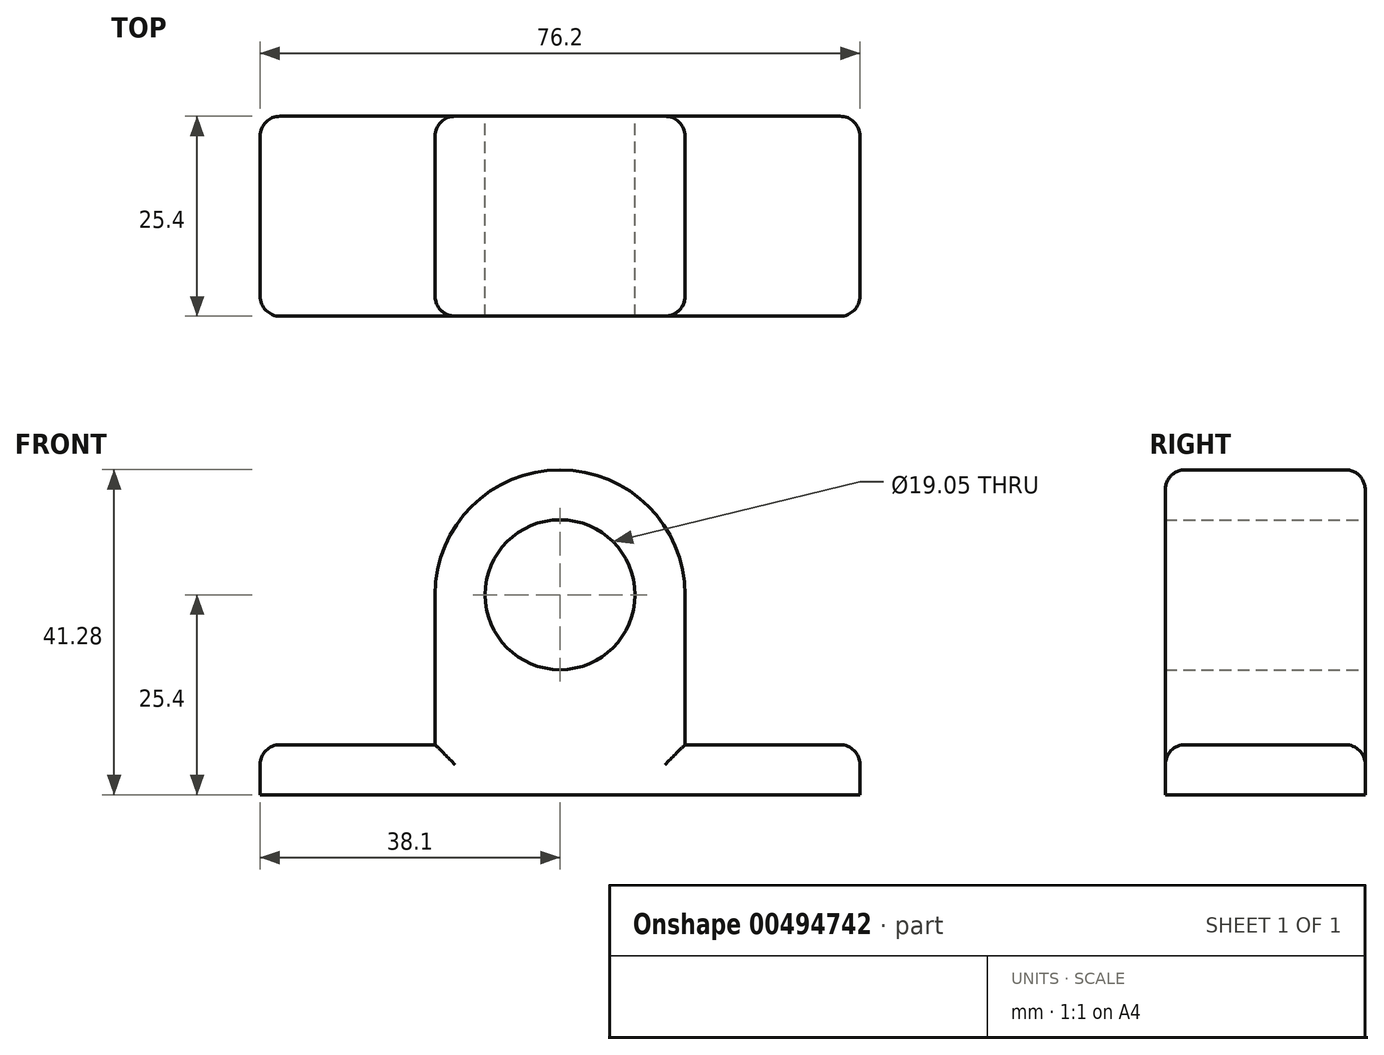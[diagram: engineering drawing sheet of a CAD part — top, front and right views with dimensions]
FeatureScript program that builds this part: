
annotation { "Feature Type Name" : "Feature", "Feature Type Description" : "" }
export const myFeature = defineFeature(function(context is Context, id is Id, definition is map)
    precondition{}
    {
        {
            var Q0;
            Q0=qCreatedBy(makeId("Front.planeOp"),FACE);
            var sketch = newSketch(context, id + "F0", { "sketchPlane" : qUnion([Q0])});
            skArc(sketch, "E0", {"start": v(15.88, 0) * mm, "mid": v(0, 15.88) * mm, "end": v(-15.88, 0) * mm});
            skCircle(sketch, "E1", {"center": v(0, 0) * mm, "radius": 9.53 * mm});
            skLineSegment(sketch, "E2", {"start": v(-15.88, 0) * mm, "end": v(-15.88, -19.05) * mm});
            skLineSegment(sketch, "E3", {"start": v(15.88, 0) * mm, "end": v(15.88, -19.05) * mm});
            skLineSegment(sketch, "E4", {"start": v(15.88, -19.05) * mm, "end": v(38.1, -19.05) * mm});
            skPoint(sketch, "E4.endSnap0", {"position": v(0, -19.05) * mm});
            skLineSegment(sketch, "E5", {"start": v(38.1, -19.05) * mm, "end": v(38.1, -25.4) * mm});
            skLineSegment(sketch, "E6", {"start": v(38.1, -25.4) * mm, "end": v(-38.1, -25.4) * mm});
            skLineSegment(sketch, "E7", {"start": v(-38.1, -25.4) * mm, "end": v(-38.1, -19.05) * mm});
            skLineSegment(sketch, "E8", {"start": v(-38.1, -19.05) * mm, "end": v(-15.88, -19.05) * mm});
            skLineSegment(sketch, "E9.trimOffspring", {"start": v(0, -25.4) * mm, "end": v(0, -28.45) * mm});
            skLineSegment(sketch, "E10.trimOffspring", {"start": v(0, -15.88) * mm, "end": v(0, -19.05) * mm});
            skSolve(sketch);
        }
        {
            var Q0;
            Q0 = qSketchRegion(id + "F0", true);
            extrude(context, id + "F1", {"entities" : qUnion([Q0]), "depth" : 25.4 * mm});
        }
        {
            var Q0;
            Q0=makeQuery(id+"F1.opExtrude","CAP_EDGE",EDGE,{"disambiguationData":[OSD([sQuery(id+"F0.wireOp",EDGE,"E0")])],"isStart":false});
            var Q1;
            Q1=makeQuery(id+"F1.opExtrude","CAP_EDGE",EDGE,{"disambiguationData":[OSD([sQuery(id+"F0.wireOp",EDGE,"E0")])],"isStart":true});
            var Q2;
            Q2=makeQuery(id+"F1.opExtrude","CAP_EDGE",EDGE,{"disambiguationData":[OSD([sQuery(id+"F0.wireOp",EDGE,"E2")])],"isStart":false});
            var Q3;
            Q3=makeQuery(id+"F1.opExtrude","CAP_EDGE",EDGE,{"disambiguationData":[OSD([sQuery(id+"F0.wireOp",EDGE,"E3")])],"isStart":false});
            var Q4;
            Q4=makeQuery(id+"F1.opExtrude","CAP_EDGE",EDGE,{"disambiguationData":[OSD([sQuery(id+"F0.wireOp",EDGE,"E4")])],"isStart":false});
            var Q5;
            Q5=makeQuery(id+"F1.opExtrude","CAP_EDGE",EDGE,{"disambiguationData":[OSD([sQuery(id+"F0.wireOp",EDGE,"E8")])],"isStart":false});
            var Q6;
            Q6=makeQuery(id+"F1.opExtrude","SWEPT_EDGE",EDGE,{"disambiguationData":[OSD([sQuery(id+"F0.wireOp",EDGE,"E7"),sQuery(id+"F0.wireOp",EDGE,"E8")])]});
            var Q7;
            Q7=makeQuery(id+"F1.opExtrude","CAP_EDGE",EDGE,{"disambiguationData":[OSD([sQuery(id+"F0.wireOp",EDGE,"E8")])],"isStart":true});
            var Q8;
            Q8=makeQuery(id+"F1.opExtrude","CAP_EDGE",EDGE,{"disambiguationData":[OSD([sQuery(id+"F0.wireOp",EDGE,"E2")])],"isStart":true});
            var Q9;
            Q9=makeQuery(id+"F1.opExtrude","CAP_EDGE",EDGE,{"disambiguationData":[OSD([sQuery(id+"F0.wireOp",EDGE,"E3")])],"isStart":true});
            var Q10;
            Q10=makeQuery(id+"F1.opExtrude","CAP_EDGE",EDGE,{"disambiguationData":[OSD([sQuery(id+"F0.wireOp",EDGE,"E4")])],"isStart":true});
            var Q11;
            Q11=makeQuery(id+"F1.opExtrude","SWEPT_EDGE",EDGE,{"disambiguationData":[OSD([sQuery(id+"F0.wireOp",EDGE,"E4"),sQuery(id+"F0.wireOp",EDGE,"E5")])]});
            var Q12;
            Q12=makeQuery(id+"F1.opExtrude","CAP_EDGE",EDGE,{"disambiguationData":[OSD([sQuery(id+"F0.wireOp",EDGE,"E7")])],"isStart":false});
            var Q13;
            Q13=makeQuery(id+"F1.opExtrude","CAP_EDGE",EDGE,{"disambiguationData":[OSD([sQuery(id+"F0.wireOp",EDGE,"E7")])],"isStart":true});
            var Q14;
            Q14=makeQuery(id+"F1.opExtrude","CAP_EDGE",EDGE,{"disambiguationData":[OSD([sQuery(id+"F0.wireOp",EDGE,"E5")])],"isStart":true});
            var Q15;
            Q15=makeQuery(id+"F1.opExtrude","CAP_EDGE",EDGE,{"disambiguationData":[OSD([sQuery(id+"F0.wireOp",EDGE,"E5")])],"isStart":false});
            fillet(context, id + "F2", {"entities" : qUnion([Q0, Q1, Q2, Q3, Q4, Q5, Q6, Q7, Q8, Q9, Q10, Q11, Q12, Q13, Q14, Q15]), "radius" : 2.54 * mm, "tangentPropagation" : true, "allowEdgeOverflow" : false});
        }
    });
